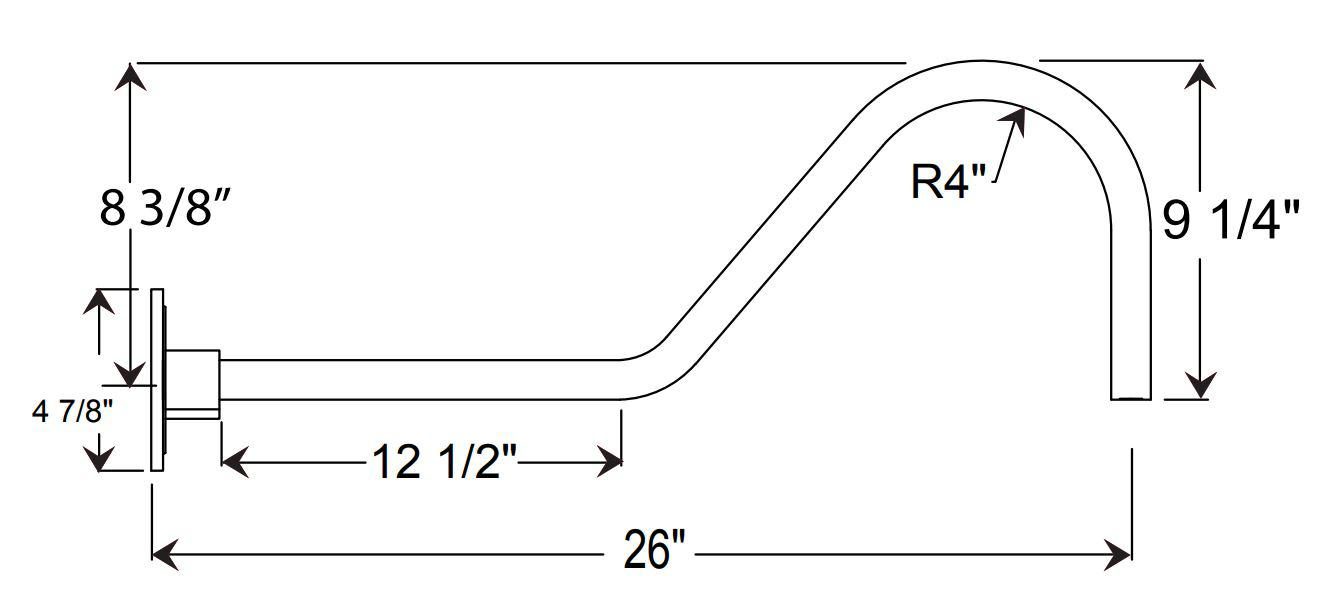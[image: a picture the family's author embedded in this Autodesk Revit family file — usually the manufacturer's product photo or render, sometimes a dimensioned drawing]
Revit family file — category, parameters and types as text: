
# Revit family: Orbitor 100w -12,16 LED
name_source: partatom
category: Lighting Fixtures
units: mm (PartAtom-declared; Revit-internal decimal feet)

## family parameters
Always vertical = Yes
Cut with Voids When Loaded = No
Light Source = Yes
OmniClass Number = 23.80.70.00
OmniClass Title = Lighting
Part Type = Normal
Room Calculation Point = No
Round Connector Dimension = Use Diameter
Shared = No
Work Plane-Based = No

## types (2) — shared parameters
Apparent Load = 16 VA
Body Colour = Spun aluminium
Body Material = body
Bulb = Bulb
CRI = >90
Color Filter = 16777215
Construction Material = Heavy Duty spun aluminum.
Default Elevation = 0' - 0"
Description = 120-277 Voltage
Dimming = 1%
Dimming Lamp Color Temperature Shift = <None>
Efficiency = 65-125 lumens per watt
INSIDE BODY = INSIDE BODY
Lamp = LED
Life = L70 50,000 hours
Load Classification = Lighting
Manufacturer = ANP Lighting
Photometric Web File = generic.ies
Power Factor = 1
Tilt Angle = 90.00°
URL = https://www.anplighting.com
Voltage = 277 V
Warranty = 5 year limited warranty
Wattage Comments = 16W
Weight = 2.0 lbs

## per-type parameters (varying)
| type | Fixture Diameter | Fixture Height | ORBT12 | ORBT16 |
| ORBT12 | 1' - 0" | 0' - 11 1/2" | Yes | No |
| ORBT16 | 1' - 4" | 1' - 0 1/2" | No | Yes |

note: column(s) folded — value = type name in every type: Model

## geometry (parser evidence)
native form markers: Sweep x21
no freeform markers — native parametric forms only
